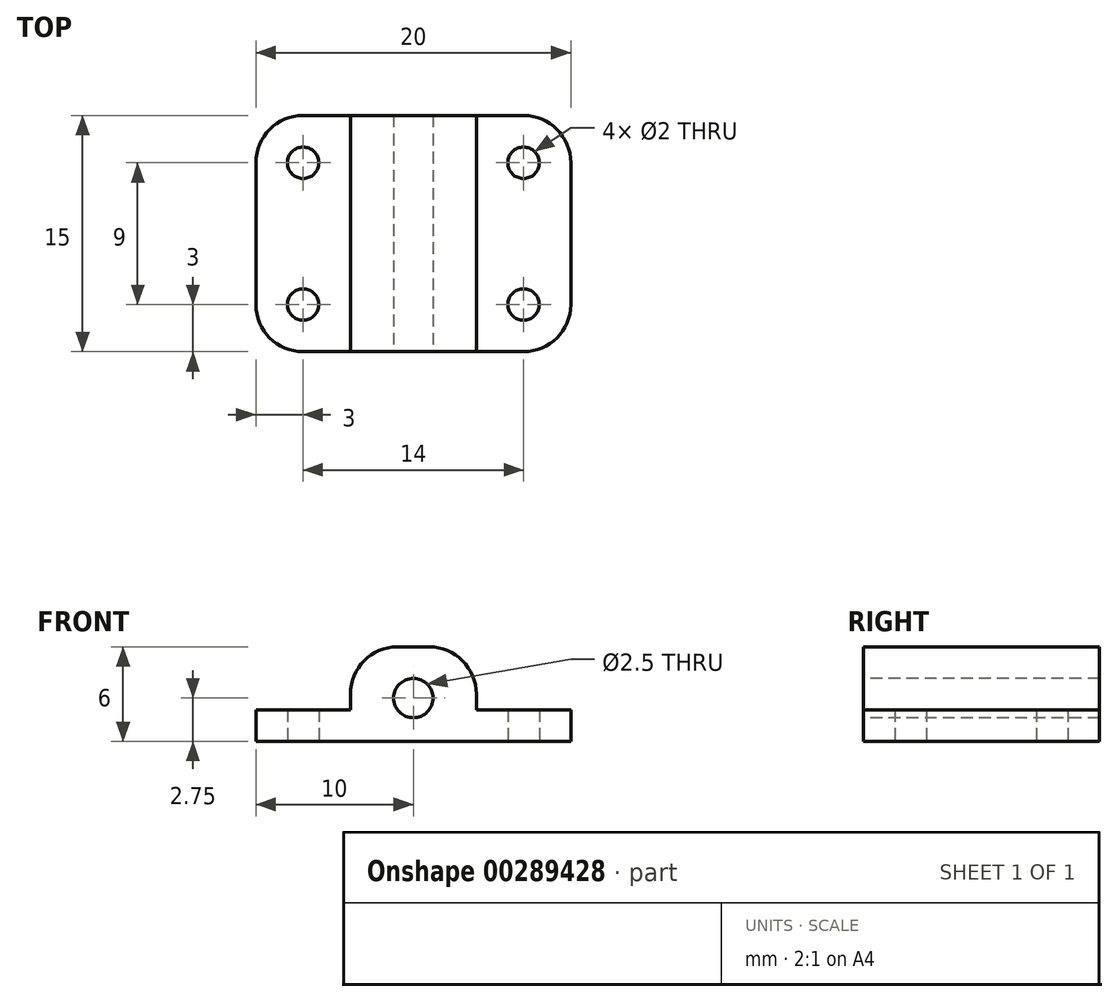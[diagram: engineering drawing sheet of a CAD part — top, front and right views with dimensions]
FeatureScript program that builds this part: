
annotation { "Feature Type Name" : "Feature", "Feature Type Description" : "" }
export const myFeature = defineFeature(function(context is Context, id is Id, definition is map)
    precondition{}
    {
        {
            var Q0;
            Q0=qCreatedBy(makeId("Top.planeOp"),FACE);
            var sketch = newSketch(context, id + "F0", { "sketchPlane" : qUnion([Q0])});
            skLineSegment(sketch, "E0.bottom", {"start": v(10, -7.5) * mm, "end": v(-10, -7.5) * mm});
            skLineSegment(sketch, "E0.top", {"start": v(10, 7.5) * mm, "end": v(-10, 7.5) * mm});
            skLineSegment(sketch, "E0.left", {"start": v(10, -7.5) * mm, "end": v(10, 7.5) * mm});
            skLineSegment(sketch, "E0.right", {"start": v(-10, -7.5) * mm, "end": v(-10, 7.5) * mm});
            skPoint(sketch, "E0.middle", {"position": v(0, 0) * mm});
            skSolve(sketch);
        }
        {
            var Q0;
            Q0 = qSketchRegion(id + "F0", true);
            extrude(context, id + "F1", {"entities" : qUnion([Q0]), "depth" : 2 * mm});
        }
        {
            var Q0;
            Q0=makeQuery(id+"F1.opExtrude","CAP_FACE",FACE,{"disambiguationData":[OSD([sQuery(id+"F0.wireOp",EDGE,"E0.bottom"),sQuery(id+"F0.wireOp",EDGE,"E0.top"),sQuery(id+"F0.wireOp",EDGE,"E0.left"),sQuery(id+"F0.wireOp",EDGE,"E0.right")])],"isStart":false});
            var sketch = newSketch(context, id + "F2", { "sketchPlane" : qUnion([Q0])});
            skLineSegment(sketch, "E1.bottom", {"start": v(4, -7.5) * mm, "end": v(-4, -7.5) * mm});
            skLineSegment(sketch, "E1.top", {"start": v(4, 7.5) * mm, "end": v(-4, 7.5) * mm});
            skLineSegment(sketch, "E1.left", {"start": v(4, -7.5) * mm, "end": v(4, 7.5) * mm});
            skLineSegment(sketch, "E1.right", {"start": v(-4, -7.5) * mm, "end": v(-4, 7.5) * mm});
            skPoint(sketch, "E1.middle", {"position": v(0, 0) * mm});
            skSolve(sketch);
        }
        {
            var Q0;
            Q0 = qSketchRegion(id + "F2", true);
            extrude(context, id + "F3", {"entities" : qUnion([Q0]), "operationType" : NewBodyOperationType.ADD, "depth" : 4 * mm});
        }
        {
            var Q0;
            Q0=makeQuery(id+"F3.boolean.opBoolean","MERGE",FACE,{"derivedFrom":[makeQuery(id+"F1.opExtrude","SWEPT_FACE",FACE,{"disambiguationData":[OSD([sQuery(id+"F0.wireOp",EDGE,"E0.bottom")])]}),makeQuery(id+"F3.opExtrude","SWEPT_FACE",FACE,{"disambiguationData":[OSD([sQuery(id+"F2.wireOp",EDGE,"E1.bottom")])]})]});
            var sketch = newSketch(context, id + "F4", { "sketchPlane" : qUnion([Q0])});
            skCircle(sketch, "E2", {"center": v(0, 2.75) * mm, "radius": 1.25 * mm});
            skSolve(sketch);
        }
        {
            var Q0;
            Q0=makeQuery(id+"F4.imprint","IMPRINT",FACE,{"disambiguationData":[TD([[makeQuery(id+"F4.imprint","IMPRINT",EDGE,{"derivedFrom":sQuery(id+"F4.wireOp",EDGE,"E2")}),1.0]])]});
            extrude(context, id + "F5", {"entities" : qUnion([Q0]), "operationType" : NewBodyOperationType.REMOVE, "endBound" : BoundingType.THROUGH_ALL, "oppositeDirection" : true, "depth" : 25 * mm});
        }
        {
            var Q0;
            Q0=makeQuery(id+"F1.opExtrude","CAP_FACE",FACE,{"disambiguationData":[OSD([sQuery(id+"F0.wireOp",EDGE,"E0.bottom"),sQuery(id+"F0.wireOp",EDGE,"E0.top"),sQuery(id+"F0.wireOp",EDGE,"E0.left"),sQuery(id+"F0.wireOp",EDGE,"E0.right")])],"isStart":true});
            var sketch = newSketch(context, id + "F6", { "sketchPlane" : qUnion([Q0])});
            skLineSegment(sketch, "E3.0", {"start": v(-7, 7.5) * mm, "end": v(-7, -7.5) * mm, "construction": true});
            skLineSegment(sketch, "E4.0", {"start": v(10, 4.5) * mm, "end": v(-10, 4.5) * mm, "construction": true});
            skCircle(sketch, "E5", {"center": v(-7, 4.5) * mm, "radius": 1 * mm});
            skCircle(sketch, "E6.MirrorC", {"center": v(7, 4.5) * mm, "radius": 1 * mm});
            skCircle(sketch, "E7.MirrorC", {"center": v(7, -4.5) * mm, "radius": 1 * mm});
            skCircle(sketch, "E8.MirrorC", {"center": v(-7, -4.5) * mm, "radius": 1 * mm});
            skSolve(sketch);
        }
        {
            var Q0;
            Q0 = qSketchRegion(id + "F6", true);
            extrude(context, id + "F7", {"entities" : qUnion([Q0]), "operationType" : NewBodyOperationType.REMOVE, "oppositeDirection" : true, "depth" : 25 * mm});
        }
        {
            var Q0;
            Q0=makeQuery(id+"F3.opExtrude","CAP_EDGE",EDGE,{"disambiguationData":[OSD([sQuery(id+"F2.wireOp",EDGE,"E1.left")])],"isStart":false});
            var Q1;
            Q1=makeQuery(id+"F3.opExtrude","CAP_EDGE",EDGE,{"disambiguationData":[OSD([sQuery(id+"F2.wireOp",EDGE,"E1.right")])],"isStart":false});
            var Q2;
            Q2=makeQuery(id+"F1.opExtrude","SWEPT_EDGE",EDGE,{"disambiguationData":[OSD([sQuery(id+"F0.wireOp",EDGE,"E0.bottom"),sQuery(id+"F0.wireOp",EDGE,"E0.left")])]});
            var Q3;
            Q3=makeQuery(id+"F1.opExtrude","SWEPT_EDGE",EDGE,{"disambiguationData":[OSD([sQuery(id+"F0.wireOp",EDGE,"E0.top"),sQuery(id+"F0.wireOp",EDGE,"E0.left")])]});
            var Q4;
            Q4=makeQuery(id+"F1.opExtrude","SWEPT_EDGE",EDGE,{"disambiguationData":[OSD([sQuery(id+"F0.wireOp",EDGE,"E0.bottom"),sQuery(id+"F0.wireOp",EDGE,"E0.right")])]});
            var Q5;
            Q5=makeQuery(id+"F1.opExtrude","SWEPT_EDGE",EDGE,{"disambiguationData":[OSD([sQuery(id+"F0.wireOp",EDGE,"E0.top"),sQuery(id+"F0.wireOp",EDGE,"E0.right")])]});
            fillet(context, id + "F8", {"entities" : qUnion([Q0, Q1, Q2, Q3, Q4, Q5]), "radius" : 3 * mm, "tangentPropagation" : true, "allowEdgeOverflow" : false});
        }
    });
